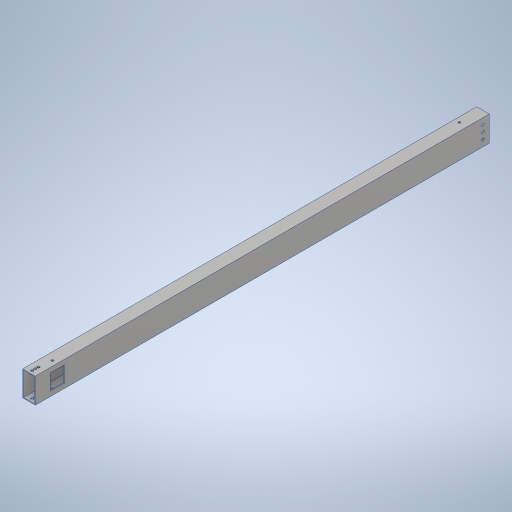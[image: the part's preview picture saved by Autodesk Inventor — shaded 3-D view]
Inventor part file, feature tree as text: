
AUTODESK INVENTOR PART (.ipt)
format: ipt  version: 2023.4 (Build 274418000, 418)  size: 316,928 bytes
history: native  units: in
note: dims shown in document units (in); Inventor stores cm internally (conversion verified against a paired STEP export)
features: sketch x6, hole x4, extrude x3
ambient origin geometry x8: Origin, YZ Plane, XZ Plane, XY Plane, X Axis, Y Axis, Z Axis, Center Point
bodies: Solid1 (feature_tree)
feature tree (13):
  extrude  "Extrusion1"  Depth=0.25in
  hole  "Hole1"  [1 undecoded]
  hole  "Hole2"  [1 undecoded]
  hole  "Hole3"  [1 undecoded]
  hole  "Hole4"  [1 undecoded]
  extrude  "Extrusion2"  Depth=0.0625in
  extrude  "Extrusion3"  Depth=0.0625in
  sketch  "Sketch2"  dims[d4=0.0in d5=0.25in]
  sketch  "Sketch3"  dims[d6=0.25in d7=0.25in]
  sketch  "Sketch4"  dims[d8=0.201in d9=0.38in d10=0.385in d11=0.25in d12=0.5635in d13=1.0in d14=0.8108in d15=0.5in]
  sketch  "Sketch5"  dims[d16=0.5in d17=0.5in]
  sketch  "Sketch6"  dims[d18=0.201in d19=0.75in d20=0.385in d21=0.25in d22=0.5635in d23=1.0in d24=0.8108in d26=1.0in]
  sketch  "Sketch7"  dims[d27=0.175in d28=0.75in d29=0.385in d30=0.25in d31=0.5635in d32=1.0in d33=0.8108in d34=0.391in d35=1.75in d36=0.391in d37=0.175in d38=0.75in d39=0.375in d40=0.25in d41=0.5635in d42=1.0in d43=0.8108in d44=1.2in d45=1.1in d47=1.25in d48=0.0625in d49=0.0in d50=1.2in d51=1.25in d52=1.1in d53=0.0625in d54=0.0in]
note: 4 required parameter values undecoded (feature->parameter linkage not recoverable at this tier; creation-order binding heuristic only, values carry confidence <= 0.55)
